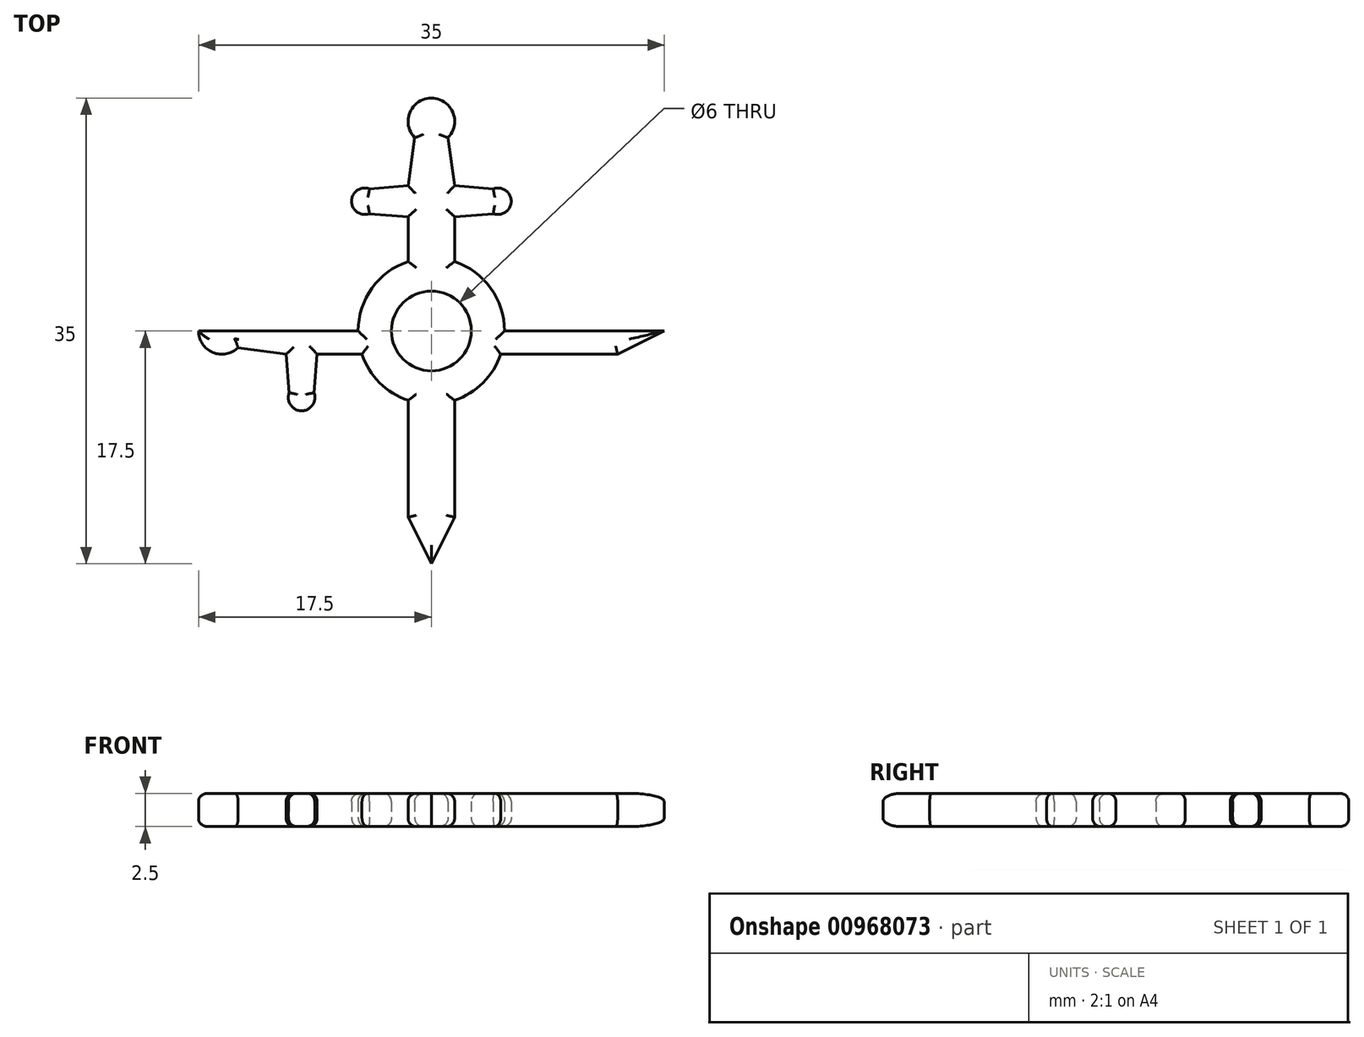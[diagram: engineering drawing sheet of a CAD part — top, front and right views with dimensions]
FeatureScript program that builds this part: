
annotation { "Feature Type Name" : "Feature", "Feature Type Description" : "" }
export const myFeature = defineFeature(function(context is Context, id is Id, definition is map)
    precondition{}
    {
        {
            assignVariable(context, id + "F0", {"name" : "thickness", "anyValue" : 2.5});
        }
        {
            var Q0;
            Q0=qCreatedBy(makeId("Front.planeOp"),FACE);
            var sketch = newSketch(context, id + "F1", { "sketchPlane" : qUnion([Q0])});
            skLineSegment(sketch, "E0", {"start": v(0, -0.36) * mm, "end": v(0, 0.53) * mm, "construction": true});
            skSolve(sketch);
        }
        {
            var Q0;
            Q0=qCreatedBy(makeId("Top.planeOp"),FACE);
            var sketch = newSketch(context, id + "F2", { "sketchPlane" : qUnion([Q0])});
            skArc(sketch, "E1", {"start": v(-1.75, 5.21) * mm, "mid": v(-5.5, 0) * mm, "end": v(-1.75, -5.21) * mm});
            skArc(sketch, "E2", {"start": v(0, 3) * mm, "mid": v(-3, 0) * mm, "end": v(0, -3) * mm});
            skLineSegment(sketch, "E3.left", {"start": v(0, 15.75) * mm, "end": v(0, 5.5) * mm});
            skLineSegment(sketch, "E4.left", {"start": v(0, 9.75) * mm, "end": v(0, 5.5) * mm});
            skLineSegment(sketch, "E5.left", {"start": v(0, 15.75) * mm, "end": v(0, 9.75) * mm});
            skArc(sketch, "E6", {"start": v(0, 17.5) * mm, "mid": v(-1.61, 16.43) * mm, "end": v(-1.25, 14.53) * mm});
            skLineSegment(sketch, "E7", {"start": v(0, -5.5) * mm, "end": v(0, -17.5) * mm});
            skLineSegment(sketch, "E8", {"start": v(0, -17.5) * mm, "end": v(-1.75, -14) * mm});
            skLineSegment(sketch, "E9", {"start": v(-1.75, -14) * mm, "end": v(-1.75, -5.21) * mm});
            skLineSegment(sketch, "E10", {"start": v(-1.75, 5.21) * mm, "end": v(-1.75, 8.58) * mm});
            skLineSegment(sketch, "E11", {"start": v(-1.75, 8.58) * mm, "end": v(-4.65, 8.81) * mm});
            skLineSegment(sketch, "E12", {"start": v(-4.65, 10.69) * mm, "end": v(-1.75, 10.92) * mm});
            skLineSegment(sketch, "E13", {"start": v(-1.75, 10.92) * mm, "end": v(-1.25, 14.53) * mm});
            skArc(sketch, "E14", {"start": v(-4.65, 10.69) * mm, "mid": v(-6, 9.75) * mm, "end": v(-4.65, 8.81) * mm});
            skLineSegment(sketch, "E15", {"start": v(-5, 9.75) * mm, "end": v(0, 9.75) * mm, "construction": true});
            skPoint(sketch, "E16", {"position": v(-4.65, 10.69) * mm});
            skPoint(sketch, "E17", {"position": v(-4.65, 8.81) * mm});
            skLineSegment(sketch, "E18", {"start": v(-1.75, 10.92) * mm, "end": v(-1.75, 8.58) * mm, "construction": true});
            skLineSegment(sketch, "E19", {"start": v(0, 5.5) * mm, "end": v(0, 3) * mm});
            skLineSegment(sketch, "E20.trimOffspring", {"start": v(0, -3) * mm, "end": v(0, -5.5) * mm});
            skPoint(sketch, "E21.orphan", {"position": v(-5, 10.66) * mm});
            skPoint(sketch, "E22.orphan", {"position": v(-5, 8.84) * mm});
            skLineSegment(sketch, "E23", {"start": v(0, 17.5) * mm, "end": v(0, 14) * mm});
            skSolve(sketch);
        }
        {
            var Q0;
            Q0 = qSketchRegion(id + "F2", true);
            extrude(context, id + "F3", {"entities" : qUnion([Q0]), "depth" : (getVariable(context, 'thickness')) * mm, "offsetDistance" : 25 * mm});
        }
        {
            var Q0;
            Q0=makeQuery(id+"F3.opExtrude","SWEPT_BODY",BODY,{"disambiguationData":[OSD([sQuery(id+"F2.wireOp",EDGE,"E1"),sQuery(id+"F2.wireOp",EDGE,"E2"),sQuery(id+"F2.wireOp",EDGE,"E4.left"),sQuery(id+"F2.wireOp",EDGE,"E5.left"),sQuery(id+"F2.wireOp",EDGE,"E6"),sQuery(id+"F2.wireOp",EDGE,"E7"),sQuery(id+"F2.wireOp",EDGE,"E8"),sQuery(id+"F2.wireOp",EDGE,"E9"),sQuery(id+"F2.wireOp",EDGE,"E10"),sQuery(id+"F2.wireOp",EDGE,"E11"),sQuery(id+"F2.wireOp",EDGE,"E12"),sQuery(id+"F2.wireOp",EDGE,"E13"),sQuery(id+"F2.wireOp",EDGE,"E14"),sQuery(id+"F2.wireOp",EDGE,"E19"),sQuery(id+"F2.wireOp",EDGE,"E20.trimOffspring"),sQuery(id+"F2.wireOp",EDGE,"E23")])]});
            var Q1;
            Q1=qCreatedBy(makeId("Right.planeOp"),FACE);
            mirror(context, id + "F4", {"entities" : qUnion([Q0]), "mirrorPlane" : qUnion([Q1])});
        }
        {
            var Q0;
            Q0=makeQuery(id+"F3.opExtrude","SWEPT_BODY",BODY,{"disambiguationData":[OSD([sQuery(id+"F2.wireOp",EDGE,"E1"),sQuery(id+"F2.wireOp",EDGE,"E2"),sQuery(id+"F2.wireOp",EDGE,"E3.left"),sQuery(id+"F2.wireOp",EDGE,"E4.left"),sQuery(id+"F2.wireOp",EDGE,"E5.left"),sQuery(id+"F2.wireOp",EDGE,"E6"),sQuery(id+"F2.wireOp",EDGE,"E7"),sQuery(id+"F2.wireOp",EDGE,"E8"),sQuery(id+"F2.wireOp",EDGE,"E9"),sQuery(id+"F2.wireOp",EDGE,"E10"),sQuery(id+"F2.wireOp",EDGE,"E11"),sQuery(id+"F2.wireOp",EDGE,"E12"),sQuery(id+"F2.wireOp",EDGE,"E13"),sQuery(id+"F2.wireOp",EDGE,"E14")])]});
            var Q1;
            Q1=sQuery(id+"F1.wireOp",EDGE,"E0");
            circularPattern(context, id + "F5", {"operationType" : NewBodyOperationType.ADD, "entities" : qUnion([Q0]), "axis" : qUnion([Q1]), "angle" : 90 * degree, "instanceCount" : 2, "equalSpace" : true});
        }
        {
            var Q0;
            {var subQ0=sQuery(id+"F5.1.F2.wireOp",EDGE,"E1");Q0=makeQuery(id+"FdIG1sQytHje1PW_3.opBoolean","MERGE",FACE,{"derivedFrom":[makeQuery(id+"F3.opExtrude","CAP_FACE",FACE,{"disambiguationData":[OSD([sQuery(id+"F2.wireOp",EDGE,"E1"),sQuery(id+"F2.wireOp",EDGE,"E2"),sQuery(id+"F2.wireOp",EDGE,"v7ZpJoOp-nusw-QLSr-9RbJ-bJiLEr91LXo7"),sQuery(id+"F2.wireOp",EDGE,"vIL4BcYA-nMGL-yGJ3-ga3U-vjNq2aGALbEF"),sQuery(id+"F2.wireOp",EDGE,"ded36fca-b699-4c9c-8e45-1f6b24a533490.MirrorCS"),sQuery(id+"F2.wireOp",EDGE,"113ruoVQ-M4KL-XzLS-Qnhd-6DCeCMZ775Q7"),sQuery(id+"F2.wireOp",EDGE,"E4.right"),sQuery(id+"F2.wireOp",EDGE,"n4rSyH3h-1NrD-ScX6-riRr-7jgFtbDAqfhq"),sQuery(id+"F2.wireOp",EDGE,"E6"),sQuery(id+"F2.wireOp",EDGE,"ce75eabf-e140-428c-91a5-72ef84fb78f10.MirrorCS"),sQuery(id+"F2.wireOp",EDGE,"14d6e69c-b8a8-4542-9b5b-1f979469ac310.MirrorCS"),sQuery(id+"F2.wireOp",EDGE,"fbd9c578-6410-4f49-8b6d-a704f98f1ad50.MirrorCS"),sQuery(id+"F2.wireOp",EDGE,"a38b117b-53eb-4dc5-a93f-0499820181ec0.MirrorCS"),sQuery(id+"F2.wireOp",EDGE,"e87fbdaf-6be0-438d-a6e1-7897cd8f2fb90.MirrorC"),sQuery(id+"F2.wireOp",EDGE,"3ac102b6-e1ec-459a-9db9-2dd38266f8ac0.MirrorCS"),sQuery(id+"F2.wireOp",EDGE,"a1574d3b-a5dd-4b71-a9ed-16474a823ba0.trimOffspring"),sQuery(id+"F2.wireOp",EDGE,"586c9f6e-5c17-4a3d-9881-5d2215f88811.trimOffspring")])],"isStart":true}),makeQuery(id+"F3.opExtrude","CAP_FACE",FACE,{"disambiguationData":[OSD([subQ0,sQuery(id+"F5.1.F2.wireOp",EDGE,"vIL4BcYA-nMGL-yGJ3-ga3U-vjNq2aGALbEF"),sQuery(id+"F5.1.F2.wireOp",EDGE,"ded36fca-b699-4c9c-8e45-1f6b24a533490.MirrorCS"),sQuery(id+"F5.1.F2.wireOp",EDGE,"113ruoVQ-M4KL-XzLS-Qnhd-6DCeCMZ775Q7"),sQuery(id+"F5.1.F2.wireOp",EDGE,"E4.right"),sQuery(id+"F5.1.F2.wireOp",EDGE,"n4rSyH3h-1NrD-ScX6-riRr-7jgFtbDAqfhq"),sQuery(id+"F5.1.F2.wireOp",EDGE,"E6"),sQuery(id+"F5.1.F2.wireOp",EDGE,"ce75eabf-e140-428c-91a5-72ef84fb78f10.MirrorCS"),sQuery(id+"F5.1.F2.wireOp",EDGE,"14d6e69c-b8a8-4542-9b5b-1f979469ac310.MirrorCS"),sQuery(id+"F5.1.F2.wireOp",EDGE,"fbd9c578-6410-4f49-8b6d-a704f98f1ad50.MirrorCS"),sQuery(id+"F5.1.F2.wireOp",EDGE,"a38b117b-53eb-4dc5-a93f-0499820181ec0.MirrorCS"),sQuery(id+"F5.1.F2.wireOp",EDGE,"e87fbdaf-6be0-438d-a6e1-7897cd8f2fb90.MirrorC")])],"isStart":true}),makeQuery(id+"F3.opExtrude","CAP_FACE",FACE,{"disambiguationData":[OSD([subQ0,sQuery(id+"F5.1.F2.wireOp",EDGE,"v7ZpJoOp-nusw-QLSr-9RbJ-bJiLEr91LXo7"),sQuery(id+"F5.1.F2.wireOp",EDGE,"3ac102b6-e1ec-459a-9db9-2dd38266f8ac0.MirrorCS"),sQuery(id+"F5.1.F2.wireOp",EDGE,"a1574d3b-a5dd-4b71-a9ed-16474a823ba0.trimOffspring"),sQuery(id+"F5.1.F2.wireOp",EDGE,"586c9f6e-5c17-4a3d-9881-5d2215f88811.trimOffspring")])],"isStart":true})]});}
            var Q1;
            {var subQ0=sQuery(id+"F5.1.F2.wireOp",EDGE,"E1");Q1=makeQuery(id+"FdIG1sQytHje1PW_3.opBoolean","MERGE",FACE,{"derivedFrom":[makeQuery(id+"F3.opExtrude","CAP_FACE",FACE,{"disambiguationData":[OSD([sQuery(id+"F2.wireOp",EDGE,"E1"),sQuery(id+"F2.wireOp",EDGE,"E2"),sQuery(id+"F2.wireOp",EDGE,"v7ZpJoOp-nusw-QLSr-9RbJ-bJiLEr91LXo7"),sQuery(id+"F2.wireOp",EDGE,"vIL4BcYA-nMGL-yGJ3-ga3U-vjNq2aGALbEF"),sQuery(id+"F2.wireOp",EDGE,"ded36fca-b699-4c9c-8e45-1f6b24a533490.MirrorCS"),sQuery(id+"F2.wireOp",EDGE,"113ruoVQ-M4KL-XzLS-Qnhd-6DCeCMZ775Q7"),sQuery(id+"F2.wireOp",EDGE,"E4.right"),sQuery(id+"F2.wireOp",EDGE,"n4rSyH3h-1NrD-ScX6-riRr-7jgFtbDAqfhq"),sQuery(id+"F2.wireOp",EDGE,"E6"),sQuery(id+"F2.wireOp",EDGE,"ce75eabf-e140-428c-91a5-72ef84fb78f10.MirrorCS"),sQuery(id+"F2.wireOp",EDGE,"14d6e69c-b8a8-4542-9b5b-1f979469ac310.MirrorCS"),sQuery(id+"F2.wireOp",EDGE,"fbd9c578-6410-4f49-8b6d-a704f98f1ad50.MirrorCS"),sQuery(id+"F2.wireOp",EDGE,"a38b117b-53eb-4dc5-a93f-0499820181ec0.MirrorCS"),sQuery(id+"F2.wireOp",EDGE,"e87fbdaf-6be0-438d-a6e1-7897cd8f2fb90.MirrorC"),sQuery(id+"F2.wireOp",EDGE,"3ac102b6-e1ec-459a-9db9-2dd38266f8ac0.MirrorCS"),sQuery(id+"F2.wireOp",EDGE,"a1574d3b-a5dd-4b71-a9ed-16474a823ba0.trimOffspring"),sQuery(id+"F2.wireOp",EDGE,"586c9f6e-5c17-4a3d-9881-5d2215f88811.trimOffspring")])],"isStart":false}),makeQuery(id+"F3.opExtrude","CAP_FACE",FACE,{"disambiguationData":[OSD([subQ0,sQuery(id+"F5.1.F2.wireOp",EDGE,"vIL4BcYA-nMGL-yGJ3-ga3U-vjNq2aGALbEF"),sQuery(id+"F5.1.F2.wireOp",EDGE,"ded36fca-b699-4c9c-8e45-1f6b24a533490.MirrorCS"),sQuery(id+"F5.1.F2.wireOp",EDGE,"113ruoVQ-M4KL-XzLS-Qnhd-6DCeCMZ775Q7"),sQuery(id+"F5.1.F2.wireOp",EDGE,"E4.right"),sQuery(id+"F5.1.F2.wireOp",EDGE,"n4rSyH3h-1NrD-ScX6-riRr-7jgFtbDAqfhq"),sQuery(id+"F5.1.F2.wireOp",EDGE,"E6"),sQuery(id+"F5.1.F2.wireOp",EDGE,"ce75eabf-e140-428c-91a5-72ef84fb78f10.MirrorCS"),sQuery(id+"F5.1.F2.wireOp",EDGE,"14d6e69c-b8a8-4542-9b5b-1f979469ac310.MirrorCS"),sQuery(id+"F5.1.F2.wireOp",EDGE,"fbd9c578-6410-4f49-8b6d-a704f98f1ad50.MirrorCS"),sQuery(id+"F5.1.F2.wireOp",EDGE,"a38b117b-53eb-4dc5-a93f-0499820181ec0.MirrorCS"),sQuery(id+"F5.1.F2.wireOp",EDGE,"e87fbdaf-6be0-438d-a6e1-7897cd8f2fb90.MirrorC")])],"isStart":false}),makeQuery(id+"F3.opExtrude","CAP_FACE",FACE,{"disambiguationData":[OSD([subQ0,sQuery(id+"F5.1.F2.wireOp",EDGE,"v7ZpJoOp-nusw-QLSr-9RbJ-bJiLEr91LXo7"),sQuery(id+"F5.1.F2.wireOp",EDGE,"3ac102b6-e1ec-459a-9db9-2dd38266f8ac0.MirrorCS"),sQuery(id+"F5.1.F2.wireOp",EDGE,"a1574d3b-a5dd-4b71-a9ed-16474a823ba0.trimOffspring"),sQuery(id+"F5.1.F2.wireOp",EDGE,"586c9f6e-5c17-4a3d-9881-5d2215f88811.trimOffspring")])],"isStart":false})]});}
            fillet(context, id + "F6", {"entities" : qUnion([Q0, Q1]), "radius" : (getVariable(context, 'thickness') / 4) * mm, "tangentPropagation" : true, "allowEdgeOverflow" : false});
        }
    });
